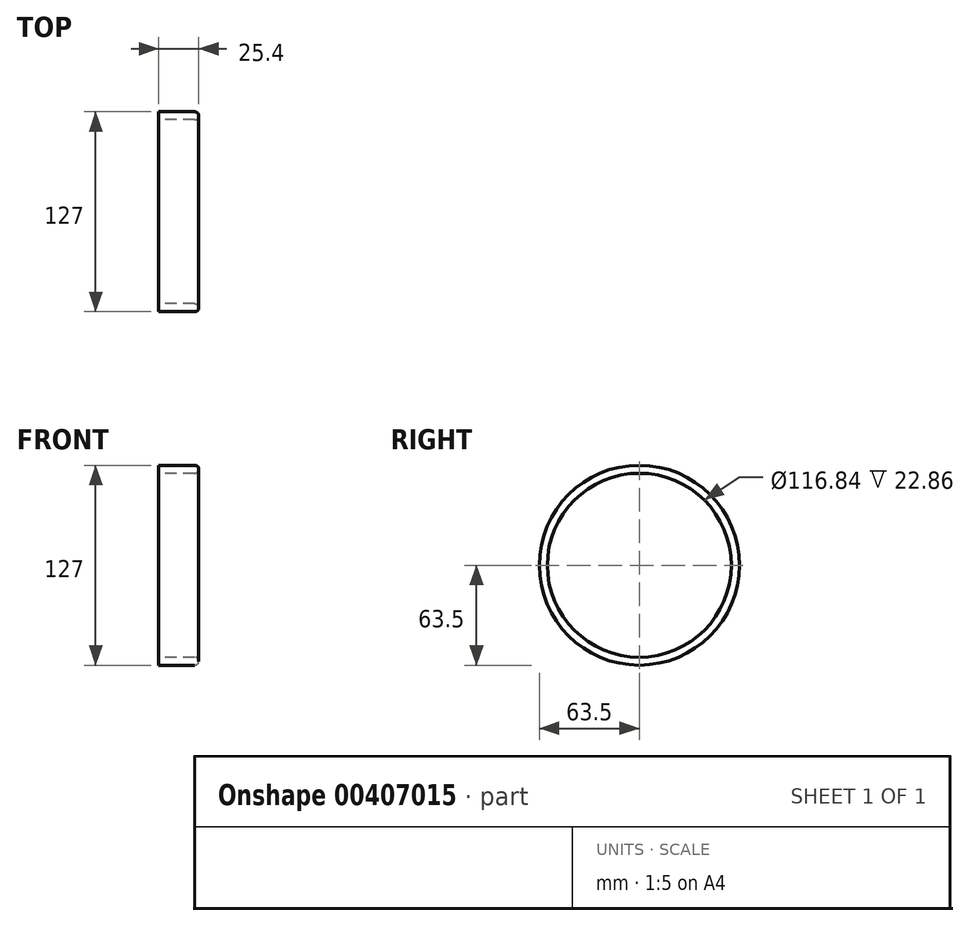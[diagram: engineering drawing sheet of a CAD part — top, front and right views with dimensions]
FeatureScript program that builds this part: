
annotation { "Feature Type Name" : "Feature", "Feature Type Description" : "" }
export const myFeature = defineFeature(function(context is Context, id is Id, definition is map)
    precondition{}
    {
        {
            var Q0;
            Q0=qCreatedBy(makeId("Right.planeOp"),FACE);
            var sketch = newSketch(context, id + "F0", { "sketchPlane" : qUnion([Q0])});
            skCircle(sketch, "E0", {"center": v(0, 0) * mm, "radius": 63.5 * mm});
            skCircle(sketch, "E1.0", {"center": v(0, 0) * mm, "radius": 58.42 * mm});
            skSolve(sketch);
        }
        {
            var Q0;
            Q0=makeQuery(id+"F0.imprint","IMPRINT",FACE,{"disambiguationData":[TD([[makeQuery(id+"F0.imprint","IMPRINT",EDGE,{"derivedFrom":sQuery(id+"F0.wireOp",EDGE,"E0")}),1.0]])]});
            extrude(context, id + "F1", {"entities" : qUnion([Q0]), "depth" : 25.4 * mm});
        }
        {
            var Q0;
            Q0=makeQuery(id+"F1.opExtrude","CAP_EDGE",EDGE,{"disambiguationData":[OSD([sQuery(id+"F0.wireOp",EDGE,"E1.0")])],"isStart":false});
            var Q1;
            Q1=makeQuery(id+"F1.opExtrude","CAP_EDGE",EDGE,{"disambiguationData":[OSD([sQuery(id+"F0.wireOp",EDGE,"E0")])],"isStart":false});
            fillet(context, id + "F2", {"entities" : qUnion([Q0, Q1]), "radius" : 2.54 * mm, "tangentPropagation" : true, "allowEdgeOverflow" : false});
        }
    });
